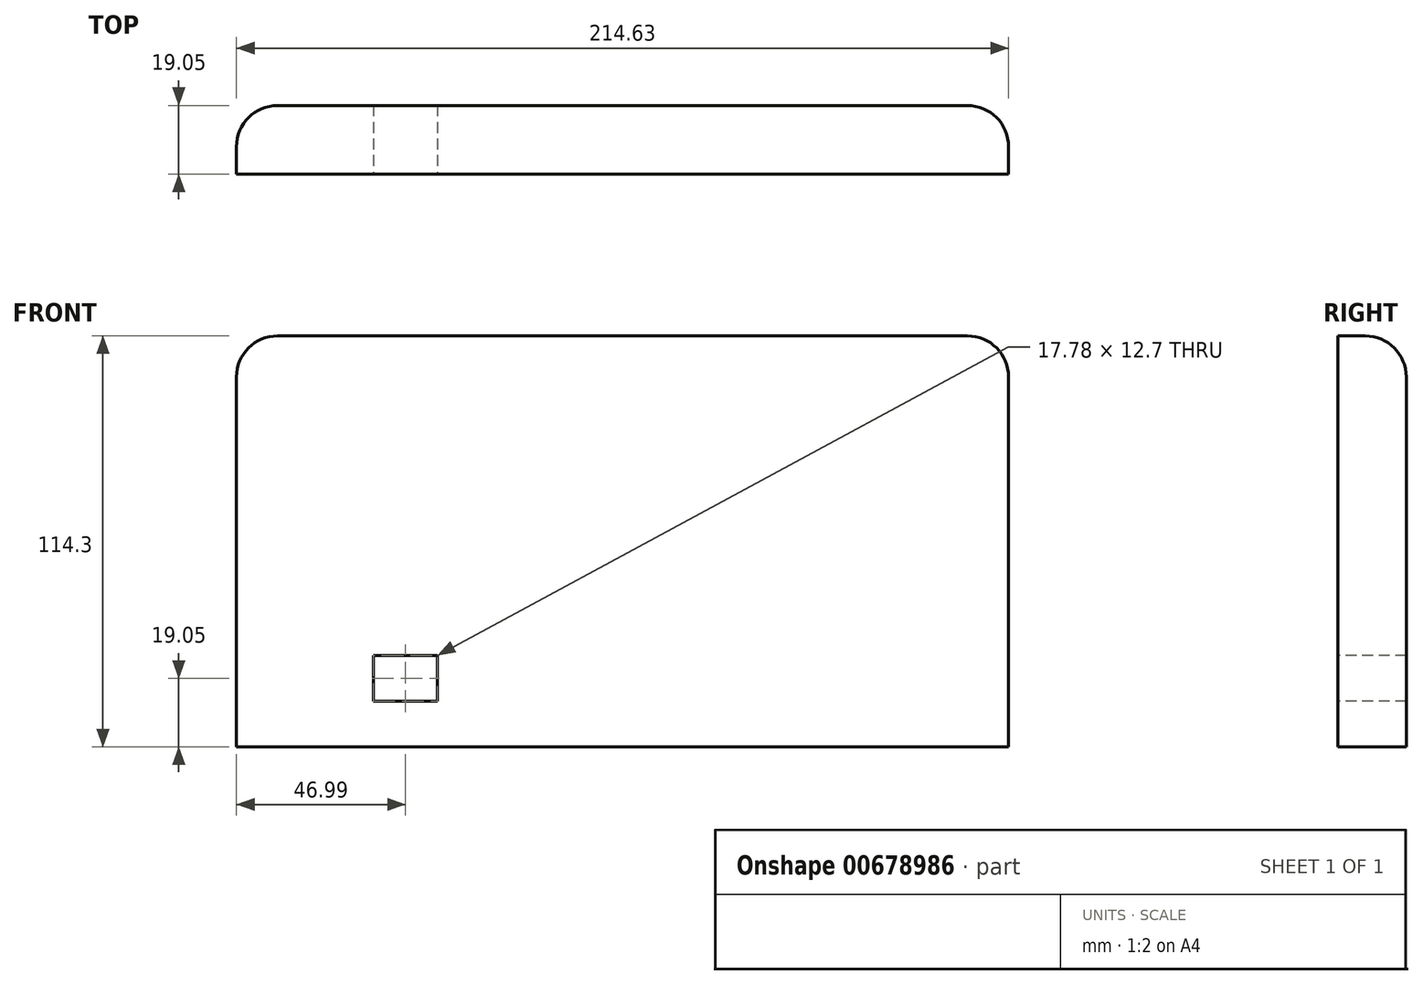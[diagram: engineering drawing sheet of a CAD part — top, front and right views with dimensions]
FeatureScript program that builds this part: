
annotation { "Feature Type Name" : "Feature", "Feature Type Description" : "" }
export const myFeature = defineFeature(function(context is Context, id is Id, definition is map)
    precondition{}
    {
        {
            var Q0;
            Q0=qCreatedBy(makeId("Front.planeOp"),FACE);
            var sketch = newSketch(context, id + "F0", { "sketchPlane" : qUnion([Q0])});
            skLineSegment(sketch, "E0.bottom", {"start": v(0, 0) * mm, "end": v(214.63, 0) * mm});
            skLineSegment(sketch, "E0.top", {"start": v(11.43, 114.3) * mm, "end": v(203.2, 114.3) * mm});
            skLineSegment(sketch, "E0.left", {"start": v(0, 0) * mm, "end": v(0, 102.87) * mm});
            skLineSegment(sketch, "E0.right", {"start": v(214.63, 0) * mm, "end": v(214.63, 102.87) * mm});
            skPoint(sketch, "E1.visualSharp", {"position": v(0, 114.3) * mm});
            skArc(sketch, "E1.filletArc", {"start": v(11.43, 114.3) * mm, "mid": v(3.35, 110.95) * mm, "end": v(0, 102.87) * mm});
            skPoint(sketch, "E2.visualSharp", {"position": v(214.63, 114.3) * mm});
            skArc(sketch, "E2.filletArc", {"start": v(214.63, 102.87) * mm, "mid": v(211.28, 110.95) * mm, "end": v(203.2, 114.3) * mm});
            skSolve(sketch);
        }
        {
            var Q0;
            Q0=makeQuery(id+"F0.imprint","IMPRINT",FACE,{"disambiguationData":[TD([[makeQuery(id+"F0.imprint","IMPRINT",EDGE,{"derivedFrom":sQuery(id+"F0.wireOp",EDGE,"E0.bottom")}),1.0]])]});
            extrude(context, id + "F1", {"entities" : qUnion([Q0]), "depth" : 19.05 * mm, "offsetDistance" : 25.4 * mm});
        }
        {
            var Q0;
            Q0=makeQuery(id+"F1.opExtrude","CAP_EDGE",EDGE,{"disambiguationData":[OSD([sQuery(id+"F0.wireOp",EDGE,"E0.top")])],"isStart":true});
            fillet(context, id + "F2", {"entities" : qUnion([Q0]), "radius" : 11.43 * mm, "tangentPropagation" : true, "allowEdgeOverflow" : false});
        }
        {
            var Q0;
            Q0=makeQuery(id+"F1.opExtrude","CAP_FACE",FACE,{"disambiguationData":[OSD([sQuery(id+"F0.wireOp",EDGE,"E0.bottom"),sQuery(id+"F0.wireOp",EDGE,"E0.top"),sQuery(id+"F0.wireOp",EDGE,"E0.left"),sQuery(id+"F0.wireOp",EDGE,"E0.right"),sQuery(id+"F0.wireOp",EDGE,"E1.filletArc"),sQuery(id+"F0.wireOp",EDGE,"E2.filletArc")])],"isStart":false});
            var sketch = newSketch(context, id + "F3", { "sketchPlane" : qUnion([Q0])});
            skLineSegment(sketch, "E3", {"start": v(55.88, 12.7) * mm, "end": v(55.88, 25.4) * mm});
            skLineSegment(sketch, "E4", {"start": v(55.88, 25.4) * mm, "end": v(38.1, 25.4) * mm});
            skLineSegment(sketch, "E5", {"start": v(38.1, 25.4) * mm, "end": v(38.1, 12.7) * mm});
            skLineSegment(sketch, "E6", {"start": v(38.1, 12.7) * mm, "end": v(55.88, 12.7) * mm});
            skSolve(sketch);
        }
        {
            var Q0;
            Q0 = qSketchRegion(id + "F3", true);
            extrude(context, id + "F4", {"entities" : qUnion([Q0]), "operationType" : NewBodyOperationType.REMOVE, "oppositeDirection" : true, "depth" : 25.4 * mm, "offsetDistance" : 25.4 * mm});
        }
    });
